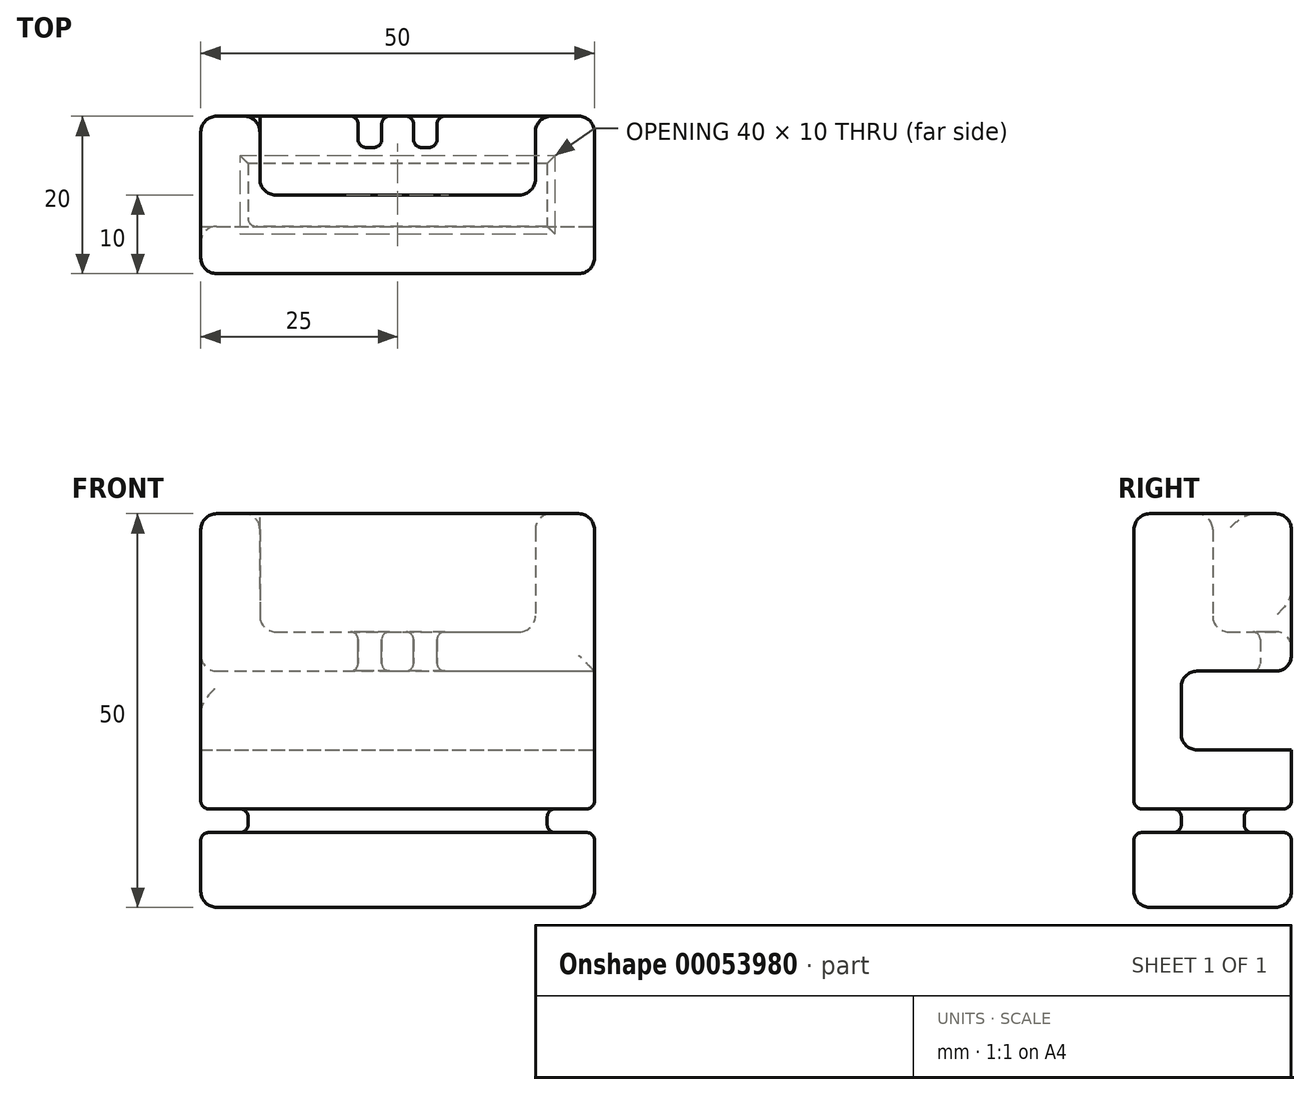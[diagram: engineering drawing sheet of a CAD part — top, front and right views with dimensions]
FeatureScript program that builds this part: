
annotation { "Feature Type Name" : "Feature", "Feature Type Description" : "" }
export const myFeature = defineFeature(function(context is Context, id is Id, definition is map)
    precondition{}
    {
        {
            var Q0;
            Q0=qCreatedBy(makeId("Front.planeOp"),FACE);
            var sketch = newSketch(context, id + "F0", { "sketchPlane" : qUnion([Q0])});
            skLineSegment(sketch, "E0.bottom", {"start": v(-25, 25) * mm, "end": v(25, 25) * mm});
            skLineSegment(sketch, "E0.top", {"start": v(-25, -25) * mm, "end": v(25, -25) * mm});
            skLineSegment(sketch, "E0.left", {"start": v(-25, 25) * mm, "end": v(-25, -25) * mm});
            skLineSegment(sketch, "E0.right", {"start": v(25, 25) * mm, "end": v(25, -25) * mm});
            skSolve(sketch);
        }
        {
            var Q0;
            Q0=makeQuery(id+"F0.imprint","IMPRINT",FACE,{"disambiguationData":[TD([[makeQuery(id+"F0.imprint","IMPRINT",EDGE,{"derivedFrom":sQuery(id+"F0.wireOp",EDGE,"E0.bottom")}),-1.0]])]});
            extrude(context, id + "F1", {"entities" : qUnion([Q0]), "endBound" : BoundingType.SYMMETRIC, "depth" : 20 * mm});
        }
        {
            var Q0;
            Q0=makeQuery(id+"F1.opExtrude","SWEPT_FACE",FACE,{"disambiguationData":[OSD([sQuery(id+"F0.wireOp",EDGE,"E0.right")])]});
            var sketch = newSketch(context, id + "F2", { "sketchPlane" : qUnion([Q0])});
            skLineSegment(sketch, "E1.bottom", {"start": v(-4, 5) * mm, "end": v(10, 5) * mm});
            skLineSegment(sketch, "E1.top", {"start": v(-4, -5) * mm, "end": v(10, -5) * mm});
            skLineSegment(sketch, "E1.left", {"start": v(-4, 5) * mm, "end": v(-4, -5) * mm});
            skLineSegment(sketch, "E1.right", {"start": v(10, 5) * mm, "end": v(10, -5) * mm});
            skSolve(sketch);
        }
        {
            var Q0;
            Q0=makeQuery(id+"F2.imprint","IMPRINT",FACE,{"disambiguationData":[TD([[makeQuery(id+"F2.imprint","IMPRINT",EDGE,{"derivedFrom":sQuery(id+"F2.wireOp",EDGE,"E1.bottom")}),-1.0]])]});
            extrude(context, id + "F3", {"entities" : qUnion([Q0]), "operationType" : NewBodyOperationType.REMOVE, "oppositeDirection" : true, "depth" : 76.7 * mm});
        }
        {
            var Q0;
            Q0=makeQuery(id+"F1.opExtrude","CAP_EDGE",EDGE,{"disambiguationData":[OSD([sQuery(id+"F0.wireOp",EDGE,"E0.bottom")])],"isStart":true});
            var Q1;
            Q1=makeQuery(id+"F3.boolean.opBoolean","COPY",EDGE,{"derivedFrom":makeQuery(id+"F3.opExtrude","SWEPT_EDGE",EDGE,{"disambiguationData":[OSD([sQuery(id+"F2.wireOp",EDGE,"E1.top"),sQuery(id+"F2.wireOp",EDGE,"E1.left")])]})});
            var Q2;
            Q2=makeQuery(id+"F3.boolean.opBoolean","COPY",EDGE,{"derivedFrom":makeQuery(id+"F3.opExtrude","SWEPT_EDGE",EDGE,{"disambiguationData":[OSD([sQuery(id+"F2.wireOp",EDGE,"E1.bottom"),sQuery(id+"F2.wireOp",EDGE,"E1.left")])]})});
            var Q3;
            Q3=makeQuery(id+"F1.opExtrude","CAP_EDGE",EDGE,{"disambiguationData":[OSD([sQuery(id+"F0.wireOp",EDGE,"E0.bottom")])],"isStart":false});
            var Q4;
            Q4=makeQuery(id+"F3.boolean.opBoolean","COPY",EDGE,{"derivedFrom":makeQuery(id+"F3.opExtrude","SWEPT_EDGE",EDGE,{"disambiguationData":[OSD([sQuery(id+"F0.wireOp",EDGE,"E0.right"),sQuery(id+"F2.wireOp",EDGE,"E1.top"),sQuery(id+"F2.wireOp",EDGE,"E1.right")])]})});
            var Q5;
            Q5=makeQuery(id+"F1.opExtrude","CAP_EDGE",EDGE,{"disambiguationData":[OSD([sQuery(id+"F0.wireOp",EDGE,"E0.top")])],"isStart":true});
            var Q6;
            Q6=makeQuery(id+"F1.opExtrude","CAP_EDGE",EDGE,{"disambiguationData":[OSD([sQuery(id+"F0.wireOp",EDGE,"E0.top")])],"isStart":false});
            var Q7;
            Q7=makeQuery(id+"F1.opExtrude","CAP_EDGE",EDGE,{"disambiguationData":[OSD([sQuery(id+"F0.wireOp",EDGE,"E0.right")])],"isStart":false});
            var Q8;
            {var subQ0=sQuery(id+"F0.wireOp",EDGE,"E0.right");var subQ1=sQuery(id+"F0.wireOp",EDGE,"E0.top");Q8=makeQuery(id+"F3.boolean.opBoolean","SPLIT",EDGE,{"disambiguationData":[TD([makeQuery(id+"F1.opExtrude","SWEPT_FACE",FACE,{"disambiguationData":[OSD([subQ1])]})])],"derivedFrom":makeQuery(id+"F1.opExtrude","CAP_EDGE",EDGE,{"disambiguationData":[OSD([subQ0])],"isStart":true})});}
            var Q9;
            {var subQ0=sQuery(id+"F0.wireOp",EDGE,"E0.left");var subQ1=sQuery(id+"F0.wireOp",EDGE,"E0.top");Q9=makeQuery(id+"F3.boolean.opBoolean","SPLIT",EDGE,{"disambiguationData":[TD([makeQuery(id+"F1.opExtrude","SWEPT_FACE",FACE,{"disambiguationData":[OSD([subQ1])]})])],"derivedFrom":makeQuery(id+"F1.opExtrude","CAP_EDGE",EDGE,{"disambiguationData":[OSD([subQ0])],"isStart":true})});}
            var Q10;
            Q10=makeQuery(id+"F1.opExtrude","CAP_EDGE",EDGE,{"disambiguationData":[OSD([sQuery(id+"F0.wireOp",EDGE,"E0.left")])],"isStart":false});
            var Q11;
            {var subQ0=sQuery(id+"F0.wireOp",EDGE,"E0.bottom");var subQ1=sQuery(id+"F0.wireOp",EDGE,"E0.left");Q11=makeQuery(id+"F3.boolean.opBoolean","SPLIT",EDGE,{"disambiguationData":[TD([makeQuery(id+"F1.opExtrude","SWEPT_FACE",FACE,{"disambiguationData":[OSD([subQ0])]})])],"derivedFrom":makeQuery(id+"F1.opExtrude","CAP_EDGE",EDGE,{"disambiguationData":[OSD([subQ1])],"isStart":true})});}
            var Q12;
            Q12=makeQuery(id+"F1.opExtrude","SWEPT_EDGE",EDGE,{"disambiguationData":[OSD([sQuery(id+"F0.wireOp",EDGE,"E0.bottom"),sQuery(id+"F0.wireOp",EDGE,"E0.left")])]});
            var Q13;
            Q13=makeQuery(id+"F1.opExtrude","SWEPT_EDGE",EDGE,{"disambiguationData":[OSD([sQuery(id+"F0.wireOp",EDGE,"E0.bottom"),sQuery(id+"F0.wireOp",EDGE,"E0.right")])]});
            var Q14;
            {var subQ0=sQuery(id+"F0.wireOp",EDGE,"E0.bottom");var subQ1=sQuery(id+"F0.wireOp",EDGE,"E0.right");Q14=makeQuery(id+"F3.boolean.opBoolean","SPLIT",EDGE,{"disambiguationData":[TD([makeQuery(id+"F1.opExtrude","SWEPT_FACE",FACE,{"disambiguationData":[OSD([subQ0])]})])],"derivedFrom":makeQuery(id+"F1.opExtrude","CAP_EDGE",EDGE,{"disambiguationData":[OSD([subQ1])],"isStart":true})});}
            var Q15;
            Q15=makeQuery(id+"F3.boolean.opBoolean","COPY",EDGE,{"derivedFrom":makeQuery(id+"F3.opExtrude","CAP_EDGE",EDGE,{"disambiguationData":[OSD([sQuery(id+"F2.wireOp",EDGE,"E1.top")])],"isStart":true})});
            var Q16;
            Q16=makeQuery(id+"F3.boolean.opBoolean","COPY",EDGE,{"derivedFrom":makeQuery(id+"F3.opExtrude","SWEPT_EDGE",EDGE,{"disambiguationData":[OSD([sQuery(id+"F0.wireOp",EDGE,"E0.right"),sQuery(id+"F2.wireOp",EDGE,"E1.bottom"),sQuery(id+"F2.wireOp",EDGE,"E1.right")])]})});
            var Q17;
            Q17=makeQuery(id+"F3.boolean.opBoolean","INTERSECT",EDGE,{"derivedFrom":[makeQuery(id+"F1.opExtrude","SWEPT_FACE",FACE,{"disambiguationData":[OSD([sQuery(id+"F0.wireOp",EDGE,"E0.left")])]}),makeQuery(id+"F3.opExtrude","SWEPT_FACE",FACE,{"disambiguationData":[OSD([sQuery(id+"F2.wireOp",EDGE,"E1.bottom")])]})]});
            var Q18;
            Q18=makeQuery(id+"F1.opExtrude","SWEPT_EDGE",EDGE,{"disambiguationData":[OSD([sQuery(id+"F0.wireOp",EDGE,"E0.top"),sQuery(id+"F0.wireOp",EDGE,"E0.left")])]});
            var Q19;
            Q19=makeQuery(id+"F1.opExtrude","SWEPT_EDGE",EDGE,{"disambiguationData":[OSD([sQuery(id+"F0.wireOp",EDGE,"E0.top"),sQuery(id+"F0.wireOp",EDGE,"E0.right")])]});
            fillet(context, id + "F4", {"entities" : qUnion([Q0, Q1, Q2, Q3, Q4, Q5, Q6, Q7, Q8, Q9, Q10, Q11, Q12, Q13, Q14, Q15, Q16, Q17, Q18, Q19]), "radius" : 2 * mm, "tangentPropagation" : true, "allowEdgeOverflow" : false});
        }
        {
            var Q0;
            Q0=qCreatedBy(makeId("Right.planeOp"),FACE);
            var sketch = newSketch(context, id + "F5", { "sketchPlane" : qUnion([Q0])});
            skLineSegment(sketch, "E2.bottom", {"start": v(0, 30) * mm, "end": v(13.71, 30) * mm});
            skLineSegment(sketch, "E2.top", {"start": v(0, 10) * mm, "end": v(13.71, 10) * mm});
            skLineSegment(sketch, "E2.left", {"start": v(0, 30) * mm, "end": v(0, 10) * mm});
            skLineSegment(sketch, "E2.right", {"start": v(13.71, 30) * mm, "end": v(13.71, 10) * mm});
            skSolve(sketch);
        }
        {
            var Q0;
            Q0=makeQuery(id+"F5.imprint","IMPRINT",FACE,{"disambiguationData":[TD([[makeQuery(id+"F5.imprint","IMPRINT",EDGE,{"derivedFrom":sQuery(id+"F5.wireOp",EDGE,"E2.bottom")}),-1.0]])]});
            extrude(context, id + "F6", {"entities" : qUnion([Q0]), "operationType" : NewBodyOperationType.REMOVE, "endBound" : BoundingType.SYMMETRIC, "oppositeDirection" : true, "depth" : 35 * mm});
        }
        {
            var Q0;
            Q0=makeQuery(id+"F6.boolean.opBoolean","COPY",EDGE,{"derivedFrom":makeQuery(id+"F6.opExtrude","SWEPT_EDGE",EDGE,{"disambiguationData":[OSD([sQuery(id+"F5.wireOp",EDGE,"E2.top"),sQuery(id+"F5.wireOp",EDGE,"E2.left")])]})});
            var Q1;
            Q1=makeQuery(id+"F6.boolean.opBoolean","INTERSECT",EDGE,{"derivedFrom":[makeQuery(id+"F1.opExtrude","SWEPT_FACE",FACE,{"disambiguationData":[OSD([sQuery(id+"F0.wireOp",EDGE,"E0.bottom")])]}),makeQuery(id+"F6.opExtrude","SWEPT_FACE",FACE,{"disambiguationData":[OSD([sQuery(id+"F5.wireOp",EDGE,"E2.left")])]})]});
            var Q2;
            Q2=makeQuery(id+"F6.boolean.opBoolean","INTERSECT",EDGE,{"derivedFrom":[makeQuery(id+"F1.opExtrude","SWEPT_FACE",FACE,{"disambiguationData":[OSD([sQuery(id+"F0.wireOp",EDGE,"E0.bottom")])]}),makeQuery(id+"F6.opExtrude","CAP_FACE",FACE,{"disambiguationData":[OSD([sQuery(id+"F5.wireOp",EDGE,"E2.bottom"),sQuery(id+"F5.wireOp",EDGE,"E2.top"),sQuery(id+"F5.wireOp",EDGE,"E2.left"),sQuery(id+"F5.wireOp",EDGE,"E2.right")])],"isStart":true})]});
            var Q3;
            Q3=makeQuery(id+"F6.boolean.opBoolean","COPY",EDGE,{"derivedFrom":makeQuery(id+"F6.opExtrude","CAP_EDGE",EDGE,{"disambiguationData":[OSD([sQuery(id+"F5.wireOp",EDGE,"E2.top")])],"isStart":true})});
            var Q4;
            {var subQ0=sQuery(id+"F0.wireOp",EDGE,"E0.bottom");var subQ1=sQuery(id+"F0.wireOp",EDGE,"E0.left");var subQ2=sQuery(id+"F0.wireOp",EDGE,"E0.right");Q4=makeQuery(id+"F6.boolean.opBoolean","INTERSECT",EDGE,{"derivedFrom":[makeQuery(id+"F3.boolean.opBoolean","SPLIT",FACE,{"disambiguationData":[TD([makeQuery(id+"F1.opExtrude","SWEPT_FACE",FACE,{"disambiguationData":[OSD([subQ0])]})])],"derivedFrom":makeQuery(id+"F1.opExtrude","CAP_FACE",FACE,{"disambiguationData":[OSD([subQ0,sQuery(id+"F0.wireOp",EDGE,"E0.top"),subQ1,subQ2])],"isStart":true})}),makeQuery(id+"F6.opExtrude","SWEPT_FACE",FACE,{"disambiguationData":[OSD([sQuery(id+"F5.wireOp",EDGE,"E2.top")])]})]});}
            var Q5;
            Q5=makeQuery(id+"F6.boolean.opBoolean","COPY",EDGE,{"derivedFrom":makeQuery(id+"F6.opExtrude","CAP_EDGE",EDGE,{"disambiguationData":[OSD([sQuery(id+"F5.wireOp",EDGE,"E2.top")])],"isStart":false})});
            var Q6;
            Q6=makeQuery(id+"F6.boolean.opBoolean","COPY",EDGE,{"derivedFrom":makeQuery(id+"F6.opExtrude","CAP_EDGE",EDGE,{"disambiguationData":[OSD([sQuery(id+"F5.wireOp",EDGE,"E2.left")])],"isStart":false})});
            var Q7;
            Q7=makeQuery(id+"F6.boolean.opBoolean","COPY",EDGE,{"derivedFrom":makeQuery(id+"F6.opExtrude","CAP_EDGE",EDGE,{"disambiguationData":[OSD([sQuery(id+"F5.wireOp",EDGE,"E2.left")])],"isStart":true})});
            fillet(context, id + "F7", {"entities" : qUnion([Q0, Q1, Q2, Q3, Q4, Q5, Q6, Q7]), "radius" : 2 * mm, "tangentPropagation" : true, "allowEdgeOverflow" : false});
        }
        {
            var Q0;
            Q0=qCreatedBy(makeId("Top.planeOp"),FACE);
            var sketch = newSketch(context, id + "F8", { "sketchPlane" : qUnion([Q0])});
            skLineSegment(sketch, "E3.bottom", {"start": v(2.01, 11.8) * mm, "end": v(5.01, 11.8) * mm});
            skLineSegment(sketch, "E3.top", {"start": v(2.01, 6.04) * mm, "end": v(5.01, 6.04) * mm});
            skLineSegment(sketch, "E3.left", {"start": v(2.01, 11.8) * mm, "end": v(2.01, 6.04) * mm});
            skLineSegment(sketch, "E3.right", {"start": v(5.01, 11.8) * mm, "end": v(5.01, 6.04) * mm});
            skLineSegment(sketch, "E4.MirrorCS", {"start": v(-2.01, 6.04) * mm, "end": v(-5.01, 6.04) * mm});
            skLineSegment(sketch, "E5.MirrorCS", {"start": v(-5.01, 11.8) * mm, "end": v(-5.01, 6.04) * mm});
            skLineSegment(sketch, "E6.MirrorCS", {"start": v(-2.01, 11.8) * mm, "end": v(-5.01, 11.8) * mm});
            skLineSegment(sketch, "E7.MirrorCS", {"start": v(-2.01, 11.8) * mm, "end": v(-2.01, 6.04) * mm});
            skSolve(sketch);
        }
        {
            var Q0;
            Q0=makeQuery(id+"F8.imprint","IMPRINT",FACE,{"disambiguationData":[TD([[makeQuery(id+"F8.imprint","IMPRINT",EDGE,{"derivedFrom":sQuery(id+"F8.wireOp",EDGE,"E3.bottom")}),-1.0]])]});
            var Q1;
            Q1=makeQuery(id+"F8.imprint","IMPRINT",FACE,{"disambiguationData":[TD([[makeQuery(id+"F8.imprint","IMPRINT",EDGE,{"derivedFrom":sQuery(id+"F8.wireOp",EDGE,"E4.MirrorCS")}),-1.0]])]});
            extrude(context, id + "F9", {"entities" : qUnion([Q0, Q1]), "operationType" : NewBodyOperationType.REMOVE, "depth" : 29.72 * mm});
        }
        {
            var Q0;
            Q0=makeQuery(id+"F9.boolean.opBoolean","INTERSECT",EDGE,{"derivedFrom":[makeQuery(id+"F6.boolean.opBoolean","COPY",FACE,{"derivedFrom":makeQuery(id+"F6.opExtrude","SWEPT_FACE",FACE,{"disambiguationData":[OSD([sQuery(id+"F5.wireOp",EDGE,"E2.top")])]})}),makeQuery(id+"F9.opExtrude","SWEPT_FACE",FACE,{"disambiguationData":[OSD([sQuery(id+"F8.wireOp",EDGE,"E3.top")])]})]});
            var Q1;
            Q1=makeQuery(id+"F9.boolean.opBoolean","COPY",EDGE,{"derivedFrom":makeQuery(id+"F9.opExtrude","SWEPT_EDGE",EDGE,{"disambiguationData":[OSD([sQuery(id+"F8.wireOp",EDGE,"E3.top"),sQuery(id+"F8.wireOp",EDGE,"E3.left")])]})});
            var Q2;
            Q2=makeQuery(id+"F9.boolean.opBoolean","INTERSECT",EDGE,{"derivedFrom":[makeQuery(id+"F6.boolean.opBoolean","COPY",FACE,{"derivedFrom":makeQuery(id+"F6.opExtrude","SWEPT_FACE",FACE,{"disambiguationData":[OSD([sQuery(id+"F5.wireOp",EDGE,"E2.top")])]})}),makeQuery(id+"F9.opExtrude","SWEPT_FACE",FACE,{"disambiguationData":[OSD([sQuery(id+"F8.wireOp",EDGE,"E3.left")])]})]});
            var Q3;
            Q3=makeQuery(id+"F9.boolean.opBoolean","INTERSECT",EDGE,{"derivedFrom":[makeQuery(id+"F6.boolean.opBoolean","COPY",FACE,{"derivedFrom":makeQuery(id+"F6.opExtrude","SWEPT_FACE",FACE,{"disambiguationData":[OSD([sQuery(id+"F5.wireOp",EDGE,"E2.top")])]})}),makeQuery(id+"F9.opExtrude","SWEPT_FACE",FACE,{"disambiguationData":[OSD([sQuery(id+"F8.wireOp",EDGE,"E4.MirrorCS")])]})]});
            var Q4;
            Q4=makeQuery(id+"F9.boolean.opBoolean","INTERSECT",EDGE,{"derivedFrom":[makeQuery(id+"F6.boolean.opBoolean","COPY",FACE,{"derivedFrom":makeQuery(id+"F6.opExtrude","SWEPT_FACE",FACE,{"disambiguationData":[OSD([sQuery(id+"F5.wireOp",EDGE,"E2.top")])]})}),makeQuery(id+"F9.opExtrude","SWEPT_FACE",FACE,{"disambiguationData":[OSD([sQuery(id+"F8.wireOp",EDGE,"E5.MirrorCS")])]})]});
            var Q5;
            Q5=makeQuery(id+"F9.boolean.opBoolean","INTERSECT",EDGE,{"derivedFrom":[makeQuery(id+"F3.boolean.opBoolean","COPY",FACE,{"derivedFrom":makeQuery(id+"F3.opExtrude","SWEPT_FACE",FACE,{"disambiguationData":[OSD([sQuery(id+"F2.wireOp",EDGE,"E1.bottom")])]})}),makeQuery(id+"F9.opExtrude","SWEPT_FACE",FACE,{"disambiguationData":[OSD([sQuery(id+"F8.wireOp",EDGE,"E3.top")])]})]});
            var Q6;
            Q6=makeQuery(id+"F9.boolean.opBoolean","COPY",EDGE,{"derivedFrom":makeQuery(id+"F9.opExtrude","SWEPT_EDGE",EDGE,{"disambiguationData":[OSD([sQuery(id+"F8.wireOp",EDGE,"E3.top"),sQuery(id+"F8.wireOp",EDGE,"E3.right")])]})});
            var Q7;
            {var subQ0=sQuery(id+"F2.wireOp",EDGE,"E1.right");var subQ1=sQuery(id+"F2.wireOp",EDGE,"E1.bottom");var subQ2=sQuery(id+"F0.wireOp",EDGE,"E0.right");Q7=makeQuery(id+"F9.boolean.opBoolean","INTERSECT",EDGE,{"derivedFrom":[makeQuery(id+"F4.opFillet","BLEND_FACE",FACE,{"disambiguationData":[OSD([subQ2,subQ1,subQ0]),TDD([makeQuery(id+"F3.boolean.opBoolean","COPY",EDGE,{"derivedFrom":makeQuery(id+"F3.opExtrude","SWEPT_EDGE",EDGE,{"disambiguationData":[OSD([subQ2,subQ1,subQ0])]})})])]}),makeQuery(id+"F9.opExtrude","SWEPT_FACE",FACE,{"disambiguationData":[OSD([sQuery(id+"F8.wireOp",EDGE,"E3.right")])]})]});}
            var Q8;
            Q8=makeQuery(id+"F9.boolean.opBoolean","INTERSECT",EDGE,{"derivedFrom":[makeQuery(id+"F3.boolean.opBoolean","COPY",FACE,{"derivedFrom":makeQuery(id+"F3.opExtrude","SWEPT_FACE",FACE,{"disambiguationData":[OSD([sQuery(id+"F2.wireOp",EDGE,"E1.bottom")])]})}),makeQuery(id+"F9.opExtrude","SWEPT_FACE",FACE,{"disambiguationData":[OSD([sQuery(id+"F8.wireOp",EDGE,"E7.MirrorCS")])]})]});
            var Q9;
            Q9=makeQuery(id+"F9.boolean.opBoolean","INTERSECT",EDGE,{"derivedFrom":[makeQuery(id+"F3.boolean.opBoolean","COPY",FACE,{"derivedFrom":makeQuery(id+"F3.opExtrude","SWEPT_FACE",FACE,{"disambiguationData":[OSD([sQuery(id+"F2.wireOp",EDGE,"E1.bottom")])]})}),makeQuery(id+"F9.opExtrude","SWEPT_FACE",FACE,{"disambiguationData":[OSD([sQuery(id+"F8.wireOp",EDGE,"E4.MirrorCS")])]})]});
            var Q10;
            Q10=makeQuery(id+"F9.boolean.opBoolean","COPY",EDGE,{"derivedFrom":makeQuery(id+"F9.opExtrude","SWEPT_EDGE",EDGE,{"disambiguationData":[OSD([sQuery(id+"F8.wireOp",EDGE,"E4.MirrorCS"),sQuery(id+"F8.wireOp",EDGE,"E7.MirrorCS")])]})});
            var Q11;
            Q11=makeQuery(id+"F9.boolean.opBoolean","COPY",EDGE,{"derivedFrom":makeQuery(id+"F9.opExtrude","SWEPT_EDGE",EDGE,{"disambiguationData":[OSD([sQuery(id+"F8.wireOp",EDGE,"E4.MirrorCS"),sQuery(id+"F8.wireOp",EDGE,"E5.MirrorCS")])]})});
            fillet(context, id + "F10", {"entities" : qUnion([Q0, Q1, Q2, Q3, Q4, Q5, Q6, Q7, Q8, Q9, Q10, Q11]), "radius" : 1 * mm, "tangentPropagation" : true, "allowEdgeOverflow" : false});
        }
        {
            var Q0;
            {var subQ0=sQuery(id+"F0.wireOp",EDGE,"E0.top");var subQ1=sQuery(id+"F0.wireOp",EDGE,"E0.left");var subQ2=sQuery(id+"F0.wireOp",EDGE,"E0.right");Q0=makeQuery(id+"F3.boolean.opBoolean","SPLIT",FACE,{"disambiguationData":[TD([makeQuery(id+"F1.opExtrude","SWEPT_FACE",FACE,{"disambiguationData":[OSD([subQ0])]})])],"derivedFrom":makeQuery(id+"F1.opExtrude","CAP_FACE",FACE,{"disambiguationData":[OSD([sQuery(id+"F0.wireOp",EDGE,"E0.bottom"),subQ0,subQ1,subQ2])],"isStart":true})});}
            var sketch = newSketch(context, id + "F11", { "sketchPlane" : qUnion([Q0])});
            skLineSegment(sketch, "E8.bottom", {"start": v(-25, -12.5) * mm, "end": v(25, -12.5) * mm});
            skLineSegment(sketch, "E8.top", {"start": v(-25, -15.5) * mm, "end": v(25, -15.5) * mm});
            skLineSegment(sketch, "E8.left", {"start": v(-25, -12.5) * mm, "end": v(-25, -15.5) * mm});
            skLineSegment(sketch, "E8.right", {"start": v(25, -12.5) * mm, "end": v(25, -15.5) * mm});
            skSolve(sketch);
        }
        {
            var Q0;
            {var subQ0=sQuery(id+"F11.wireOp",EDGE,"E8.bottom");var subQ1=sQuery(id+"F0.wireOp",EDGE,"E0.top");var subQ2=makeQuery(id+"F1.opExtrude","SWEPT_FACE",FACE,{"disambiguationData":[OSD([subQ1])]});var subQ3=sQuery(id+"F0.wireOp",EDGE,"E0.left");var subQ5=sQuery(id+"F0.wireOp",EDGE,"E0.right");var subQ8=makeQuery(id+"F1.opExtrude","CAP_FACE",FACE,{"disambiguationData":[OSD([sQuery(id+"F0.wireOp",EDGE,"E0.bottom"),subQ1,subQ3,subQ5])],"isStart":true});var subQ9=makeQuery(id+"F3.boolean.opBoolean","SPLIT",FACE,{"disambiguationData":[TD([subQ2])],"derivedFrom":subQ8});var subQ10=makeQuery(id+"F4.opFillet","BLEND_EDGE",EDGE,{"blendedFrom":[makeQuery(id+"F3.boolean.opBoolean","SPLIT",EDGE,{"disambiguationData":[TD([subQ2])],"derivedFrom":makeQuery(id+"F1.opExtrude","CAP_EDGE",EDGE,{"disambiguationData":[OSD([subQ5])],"isStart":true})}),subQ9],"blendedInto":[subQ9]});var subQ11=makeQuery(id+"F11.imprint","INTERSECT",VERTEX,{"derivedFrom":[subQ10,subQ0]});Q0=makeQuery(id+"F11.imprint","IMPRINT",FACE,{"disambiguationData":[TD([[makeQuery(id+"F11.imprint","IMPRINT",EDGE,{"disambiguationData":[TD([[subQ11,-1.0]])],"derivedFrom":subQ0}),-1.0]])]});}
            var Q1;
            {var subQ0=sQuery(id+"F11.wireOp",EDGE,"E8.left");Q1=makeQuery(id+"F11.imprint","IMPRINT",FACE,{"disambiguationData":[TD([[makeQuery(id+"F11.imprint","IMPRINT",EDGE,{"derivedFrom":subQ0}),1.0]])]});}
            var Q2;
            {var subQ0=sQuery(id+"F11.wireOp",EDGE,"E8.right");Q2=makeQuery(id+"F11.imprint","IMPRINT",FACE,{"disambiguationData":[TD([[makeQuery(id+"F11.imprint","IMPRINT",EDGE,{"derivedFrom":subQ0}),-1.0]])]});}
            extrude(context, id + "F12", {"entities" : qUnion([Q0, Q1, Q2]), "operationType" : NewBodyOperationType.REMOVE, "oppositeDirection" : true, "depth" : 6 * mm});
        }
        {
            var Q0;
            Q0=makeQuery(id+"F1.opExtrude","SWEPT_FACE",FACE,{"disambiguationData":[OSD([sQuery(id+"F0.wireOp",EDGE,"E0.right")])]});
            var sketch = newSketch(context, id + "F13", { "sketchPlane" : qUnion([Q0])});
            skLineSegment(sketch, "E9.bottom", {"start": v(4, -15.5) * mm, "end": v(-15.57, -15.5) * mm});
            skLineSegment(sketch, "E9.top", {"start": v(4, -12.5) * mm, "end": v(-15.57, -12.5) * mm});
            skLineSegment(sketch, "E9.left", {"start": v(4, -15.5) * mm, "end": v(4, -12.5) * mm});
            skLineSegment(sketch, "E9.right", {"start": v(-15.57, -15.5) * mm, "end": v(-15.57, -12.5) * mm});
            skSolve(sketch);
        }
        {
            var Q0;
            {var subQ0=sQuery(id+"F13.wireOp",EDGE,"E9.right");Q0=makeQuery(id+"F13.imprint","IMPRINT",FACE,{"disambiguationData":[TD([[makeQuery(id+"F13.imprint","IMPRINT",EDGE,{"derivedFrom":subQ0}),-1.0]])]});}
            var Q1;
            {var subQ0=sQuery(id+"F13.wireOp",EDGE,"E9.left");Q1=makeQuery(id+"F13.imprint","IMPRINT",FACE,{"disambiguationData":[TD([[makeQuery(id+"F13.imprint","IMPRINT",EDGE,{"derivedFrom":subQ0}),-1.0]])]});}
            extrude(context, id + "F14", {"entities" : qUnion([Q0, Q1]), "operationType" : NewBodyOperationType.REMOVE, "oppositeDirection" : true, "depth" : 6 * mm});
        }
        {
            var Q0;
            Q0=makeQuery(id+"F1.opExtrude","CAP_FACE",FACE,{"disambiguationData":[OSD([sQuery(id+"F0.wireOp",EDGE,"E0.bottom"),sQuery(id+"F0.wireOp",EDGE,"E0.top"),sQuery(id+"F0.wireOp",EDGE,"E0.left"),sQuery(id+"F0.wireOp",EDGE,"E0.right")])],"isStart":false});
            var sketch = newSketch(context, id + "F15", { "sketchPlane" : qUnion([Q0])});
            skLineSegment(sketch, "E10.bottom", {"start": v(19, -15.5) * mm, "end": v(-31.6, -15.5) * mm});
            skLineSegment(sketch, "E10.top", {"start": v(19, -12.5) * mm, "end": v(-31.6, -12.5) * mm});
            skLineSegment(sketch, "E10.left", {"start": v(19, -15.5) * mm, "end": v(19, -12.5) * mm});
            skLineSegment(sketch, "E10.right", {"start": v(-31.6, -15.5) * mm, "end": v(-31.6, -12.5) * mm});
            skSolve(sketch);
        }
        {
            var Q0;
            {var subQ0=sQuery(id+"F15.wireOp",EDGE,"E10.right");Q0=makeQuery(id+"F15.imprint","IMPRINT",FACE,{"disambiguationData":[TD([[makeQuery(id+"F15.imprint","IMPRINT",EDGE,{"derivedFrom":subQ0}),-1.0]])]});}
            var Q1;
            {var subQ0=sQuery(id+"F15.wireOp",EDGE,"E10.left");Q1=makeQuery(id+"F15.imprint","IMPRINT",FACE,{"disambiguationData":[TD([[makeQuery(id+"F15.imprint","IMPRINT",EDGE,{"derivedFrom":subQ0}),1.0]])]});}
            extrude(context, id + "F16", {"entities" : qUnion([Q0, Q1]), "operationType" : NewBodyOperationType.REMOVE, "oppositeDirection" : true, "depth" : 6 * mm});
        }
        {
            var Q0;
            Q0=makeQuery(id+"F1.opExtrude","SWEPT_FACE",FACE,{"disambiguationData":[OSD([sQuery(id+"F0.wireOp",EDGE,"E0.left")])]});
            var sketch = newSketch(context, id + "F17", { "sketchPlane" : qUnion([Q0])});
            skLineSegment(sketch, "E11.bottom", {"start": v(-4, -12.5) * mm, "end": v(13.16, -12.5) * mm});
            skLineSegment(sketch, "E11.top", {"start": v(-4, -15.5) * mm, "end": v(13.16, -15.5) * mm});
            skLineSegment(sketch, "E11.left", {"start": v(-4, -12.5) * mm, "end": v(-4, -15.5) * mm});
            skLineSegment(sketch, "E11.right", {"start": v(13.16, -12.5) * mm, "end": v(13.16, -15.5) * mm});
            skSolve(sketch);
        }
        {
            var Q0;
            {var subQ0=sQuery(id+"F17.wireOp",EDGE,"E11.left");Q0=makeQuery(id+"F17.imprint","IMPRINT",FACE,{"disambiguationData":[TD([[makeQuery(id+"F17.imprint","IMPRINT",EDGE,{"derivedFrom":subQ0}),1.0]])]});}
            var Q1;
            {var subQ15=sQuery(id+"F17.wireOp",EDGE,"E11.right");Q1=makeQuery(id+"F17.imprint","IMPRINT",FACE,{"disambiguationData":[TD([[makeQuery(id+"F17.imprint","IMPRINT",EDGE,{"derivedFrom":subQ15}),-1.0]])]});}
            extrude(context, id + "F18", {"entities" : qUnion([Q0, Q1]), "operationType" : NewBodyOperationType.REMOVE, "oppositeDirection" : true, "depth" : 6 * mm});
        }
        {
            var Q0;
            Q0=makeQuery(id+"F12.boolean.opBoolean","COPY",EDGE,{"derivedFrom":makeQuery(id+"F12.opExtrude","CAP_EDGE",EDGE,{"disambiguationData":[OSD([sQuery(id+"F11.wireOp",EDGE,"E8.top")])],"isStart":true})});
            var Q1;
            Q1=makeQuery(id+"F12.boolean.opBoolean","COPY",EDGE,{"derivedFrom":makeQuery(id+"F12.opExtrude","CAP_EDGE",EDGE,{"disambiguationData":[OSD([sQuery(id+"F11.wireOp",EDGE,"E8.top")])],"isStart":false})});
            var Q2;
            Q2=makeQuery(id+"F14.boolean.opBoolean","COPY",EDGE,{"derivedFrom":makeQuery(id+"F14.opExtrude","CAP_EDGE",EDGE,{"disambiguationData":[OSD([sQuery(id+"F13.wireOp",EDGE,"E9.top")])],"isStart":false})});
            var Q3;
            Q3=makeQuery(id+"F12.boolean.opBoolean","COPY",EDGE,{"derivedFrom":makeQuery(id+"F12.opExtrude","CAP_EDGE",EDGE,{"disambiguationData":[OSD([sQuery(id+"F11.wireOp",EDGE,"E8.bottom")])],"isStart":false})});
            var Q4;
            Q4=makeQuery(id+"F12.boolean.opBoolean","COPY",EDGE,{"derivedFrom":makeQuery(id+"F12.opExtrude","CAP_EDGE",EDGE,{"disambiguationData":[OSD([sQuery(id+"F11.wireOp",EDGE,"E8.bottom")])],"isStart":true})});
            var Q5;
            {var subQ0=sQuery(id+"F0.wireOp",EDGE,"E0.right");var subQ1=sQuery(id+"F0.wireOp",EDGE,"E0.top");Q5=makeQuery(id+"F12.boolean.opBoolean","INTERSECT",EDGE,{"derivedFrom":[makeQuery(id+"F4.opFillet","BLEND_FACE",FACE,{"disambiguationData":[OSD([subQ0]),TDD([makeQuery(id+"F3.boolean.opBoolean","SPLIT",EDGE,{"disambiguationData":[TD([makeQuery(id+"F1.opExtrude","SWEPT_FACE",FACE,{"disambiguationData":[OSD([subQ1])]})])],"derivedFrom":makeQuery(id+"F1.opExtrude","CAP_EDGE",EDGE,{"disambiguationData":[OSD([subQ0])],"isStart":true})})])]}),makeQuery(id+"F12.opExtrude","SWEPT_FACE",FACE,{"disambiguationData":[OSD([sQuery(id+"F11.wireOp",EDGE,"E8.bottom")])]})]});}
            var Q6;
            Q6=makeQuery(id+"F14.boolean.opBoolean","MERGE",EDGE,{"derivedFrom":[makeQuery(id+"F12.boolean.opBoolean","COPY",EDGE,{"derivedFrom":makeQuery(id+"F12.opExtrude","SWEPT_EDGE",EDGE,{"disambiguationData":[OSD([sQuery(id+"F11.wireOp",EDGE,"E8.bottom"),sQuery(id+"F11.wireOp",EDGE,"E8.left")])]})}),makeQuery(id+"F14.opExtrude","CAP_EDGE",EDGE,{"disambiguationData":[OSD([sQuery(id+"F13.wireOp",EDGE,"E9.top")])],"isStart":true})]});
            var Q7;
            Q7=makeQuery(id+"F14.boolean.opBoolean","COPY",EDGE,{"derivedFrom":makeQuery(id+"F14.opExtrude","CAP_EDGE",EDGE,{"disambiguationData":[OSD([sQuery(id+"F13.wireOp",EDGE,"E9.left")])],"isStart":false})});
            var Q8;
            Q8=makeQuery(id+"F14.boolean.opBoolean","COPY",EDGE,{"derivedFrom":makeQuery(id+"F14.opExtrude","CAP_EDGE",EDGE,{"disambiguationData":[OSD([sQuery(id+"F13.wireOp",EDGE,"E9.bottom")])],"isStart":false})});
            var Q9;
            Q9=makeQuery(id+"F14.boolean.opBoolean","MERGE",EDGE,{"derivedFrom":[makeQuery(id+"F12.boolean.opBoolean","COPY",EDGE,{"derivedFrom":makeQuery(id+"F12.opExtrude","SWEPT_EDGE",EDGE,{"disambiguationData":[OSD([sQuery(id+"F11.wireOp",EDGE,"E8.top"),sQuery(id+"F11.wireOp",EDGE,"E8.left")])]})}),makeQuery(id+"F14.opExtrude","CAP_EDGE",EDGE,{"disambiguationData":[OSD([sQuery(id+"F13.wireOp",EDGE,"E9.bottom")])],"isStart":true})]});
            var Q10;
            {var subQ0=sQuery(id+"F0.wireOp",EDGE,"E0.right");var subQ1=sQuery(id+"F0.wireOp",EDGE,"E0.top");Q10=makeQuery(id+"F12.boolean.opBoolean","INTERSECT",EDGE,{"derivedFrom":[makeQuery(id+"F4.opFillet","BLEND_FACE",FACE,{"disambiguationData":[OSD([subQ0]),TDD([makeQuery(id+"F3.boolean.opBoolean","SPLIT",EDGE,{"disambiguationData":[TD([makeQuery(id+"F1.opExtrude","SWEPT_FACE",FACE,{"disambiguationData":[OSD([subQ1])]})])],"derivedFrom":makeQuery(id+"F1.opExtrude","CAP_EDGE",EDGE,{"disambiguationData":[OSD([subQ0])],"isStart":true})})])]}),makeQuery(id+"F12.opExtrude","SWEPT_FACE",FACE,{"disambiguationData":[OSD([sQuery(id+"F11.wireOp",EDGE,"E8.top")])]})]});}
            var Q11;
            {var subQ0=sQuery(id+"F0.wireOp",EDGE,"E0.right");Q11=makeQuery(id+"F14.boolean.opBoolean","INTERSECT",EDGE,{"derivedFrom":[makeQuery(id+"F4.opFillet","BLEND_FACE",FACE,{"disambiguationData":[OSD([subQ0]),TDD([makeQuery(id+"F1.opExtrude","CAP_EDGE",EDGE,{"disambiguationData":[OSD([subQ0])],"isStart":false})])]}),makeQuery(id+"F14.opExtrude","SWEPT_FACE",FACE,{"disambiguationData":[OSD([sQuery(id+"F13.wireOp",EDGE,"E9.bottom")])]})]});}
            var Q12;
            Q12=makeQuery(id+"F16.boolean.opBoolean","COPY",EDGE,{"derivedFrom":makeQuery(id+"F16.opExtrude","CAP_EDGE",EDGE,{"disambiguationData":[OSD([sQuery(id+"F15.wireOp",EDGE,"E10.bottom")])],"isStart":false})});
            var Q13;
            Q13=makeQuery(id+"F16.boolean.opBoolean","MERGE",EDGE,{"derivedFrom":[makeQuery(id+"F14.boolean.opBoolean","INTERSECT",EDGE,{"derivedFrom":[makeQuery(id+"F1.opExtrude","CAP_FACE",FACE,{"disambiguationData":[OSD([sQuery(id+"F0.wireOp",EDGE,"E0.bottom"),sQuery(id+"F0.wireOp",EDGE,"E0.top"),sQuery(id+"F0.wireOp",EDGE,"E0.left"),sQuery(id+"F0.wireOp",EDGE,"E0.right")])],"isStart":false}),makeQuery(id+"F14.opExtrude","SWEPT_FACE",FACE,{"disambiguationData":[OSD([sQuery(id+"F13.wireOp",EDGE,"E9.bottom")])]})]}),makeQuery(id+"F16.opExtrude","CAP_EDGE",EDGE,{"disambiguationData":[OSD([sQuery(id+"F15.wireOp",EDGE,"E10.bottom")])],"isStart":true})]});
            var Q14;
            Q14=makeQuery(id+"F16.boolean.opBoolean","COPY",EDGE,{"derivedFrom":makeQuery(id+"F16.opExtrude","CAP_EDGE",EDGE,{"disambiguationData":[OSD([sQuery(id+"F15.wireOp",EDGE,"E10.top")])],"isStart":false})});
            var Q15;
            Q15=makeQuery(id+"F16.boolean.opBoolean","MERGE",EDGE,{"derivedFrom":[makeQuery(id+"F14.boolean.opBoolean","INTERSECT",EDGE,{"derivedFrom":[makeQuery(id+"F1.opExtrude","CAP_FACE",FACE,{"disambiguationData":[OSD([sQuery(id+"F0.wireOp",EDGE,"E0.bottom"),sQuery(id+"F0.wireOp",EDGE,"E0.top"),sQuery(id+"F0.wireOp",EDGE,"E0.left"),sQuery(id+"F0.wireOp",EDGE,"E0.right")])],"isStart":false}),makeQuery(id+"F14.opExtrude","SWEPT_FACE",FACE,{"disambiguationData":[OSD([sQuery(id+"F13.wireOp",EDGE,"E9.top")])]})]}),makeQuery(id+"F16.opExtrude","CAP_EDGE",EDGE,{"disambiguationData":[OSD([sQuery(id+"F15.wireOp",EDGE,"E10.top")])],"isStart":true})]});
            var Q16;
            Q16=makeQuery(id+"F18.boolean.opBoolean","COPY",EDGE,{"derivedFrom":makeQuery(id+"F18.opExtrude","CAP_EDGE",EDGE,{"disambiguationData":[OSD([sQuery(id+"F17.wireOp",EDGE,"E11.bottom")])],"isStart":false})});
            var Q17;
            Q17=makeQuery(id+"F18.boolean.opBoolean","MERGE",EDGE,{"derivedFrom":[makeQuery(id+"F12.boolean.opBoolean","COPY",EDGE,{"derivedFrom":makeQuery(id+"F12.opExtrude","SWEPT_EDGE",EDGE,{"disambiguationData":[OSD([sQuery(id+"F11.wireOp",EDGE,"E8.bottom"),sQuery(id+"F11.wireOp",EDGE,"E8.right")])]})}),makeQuery(id+"F16.boolean.opBoolean","INTERSECT",EDGE,{"derivedFrom":[makeQuery(id+"F1.opExtrude","SWEPT_FACE",FACE,{"disambiguationData":[OSD([sQuery(id+"F0.wireOp",EDGE,"E0.left")])]}),makeQuery(id+"F16.opExtrude","SWEPT_FACE",FACE,{"disambiguationData":[OSD([sQuery(id+"F15.wireOp",EDGE,"E10.top")])]})]}),makeQuery(id+"F18.opExtrude","CAP_EDGE",EDGE,{"disambiguationData":[OSD([sQuery(id+"F17.wireOp",EDGE,"E11.bottom")])],"isStart":true})]});
            var Q18;
            {var subQ0=sQuery(id+"F0.wireOp",EDGE,"E0.left");Q18=makeQuery(id+"F16.boolean.opBoolean","INTERSECT",EDGE,{"derivedFrom":[makeQuery(id+"F4.opFillet","BLEND_FACE",FACE,{"disambiguationData":[OSD([subQ0]),TDD([makeQuery(id+"F1.opExtrude","CAP_EDGE",EDGE,{"disambiguationData":[OSD([subQ0])],"isStart":false})])]}),makeQuery(id+"F16.opExtrude","SWEPT_FACE",FACE,{"disambiguationData":[OSD([sQuery(id+"F15.wireOp",EDGE,"E10.top")])]})]});}
            var Q19;
            Q19=makeQuery(id+"F18.boolean.opBoolean","INTERSECT",EDGE,{"derivedFrom":[makeQuery(id+"F16.boolean.opBoolean","COPY",FACE,{"derivedFrom":makeQuery(id+"F16.opExtrude","CAP_FACE",FACE,{"disambiguationData":[OSD([sQuery(id+"F15.wireOp",EDGE,"E10.bottom"),sQuery(id+"F15.wireOp",EDGE,"E10.top"),sQuery(id+"F15.wireOp",EDGE,"E10.left"),sQuery(id+"F15.wireOp",EDGE,"E10.right")])],"isStart":false})}),makeQuery(id+"F18.opExtrude","CAP_FACE",FACE,{"disambiguationData":[OSD([sQuery(id+"F17.wireOp",EDGE,"E11.bottom"),sQuery(id+"F17.wireOp",EDGE,"E11.top"),sQuery(id+"F17.wireOp",EDGE,"E11.left"),sQuery(id+"F17.wireOp",EDGE,"E11.right")])],"isStart":false})]});
            var Q20;
            Q20=makeQuery(id+"F18.boolean.opBoolean","COPY",EDGE,{"derivedFrom":makeQuery(id+"F18.opExtrude","CAP_EDGE",EDGE,{"disambiguationData":[OSD([sQuery(id+"F17.wireOp",EDGE,"E11.left")])],"isStart":false})});
            var Q21;
            Q21=makeQuery(id+"F18.boolean.opBoolean","COPY",EDGE,{"derivedFrom":makeQuery(id+"F18.opExtrude","CAP_EDGE",EDGE,{"disambiguationData":[OSD([sQuery(id+"F17.wireOp",EDGE,"E11.top")])],"isStart":false})});
            var Q22;
            {var subQ0=sQuery(id+"F0.wireOp",EDGE,"E0.left");var subQ1=sQuery(id+"F0.wireOp",EDGE,"E0.top");Q22=makeQuery(id+"F12.boolean.opBoolean","INTERSECT",EDGE,{"derivedFrom":[makeQuery(id+"F4.opFillet","BLEND_FACE",FACE,{"disambiguationData":[OSD([subQ0]),TDD([makeQuery(id+"F3.boolean.opBoolean","SPLIT",EDGE,{"disambiguationData":[TD([makeQuery(id+"F1.opExtrude","SWEPT_FACE",FACE,{"disambiguationData":[OSD([subQ1])]})])],"derivedFrom":makeQuery(id+"F1.opExtrude","CAP_EDGE",EDGE,{"disambiguationData":[OSD([subQ0])],"isStart":true})})])]}),makeQuery(id+"F12.opExtrude","SWEPT_FACE",FACE,{"disambiguationData":[OSD([sQuery(id+"F11.wireOp",EDGE,"E8.top")])]})]});}
            var Q23;
            Q23=makeQuery(id+"F18.boolean.opBoolean","MERGE",EDGE,{"derivedFrom":[makeQuery(id+"F12.boolean.opBoolean","COPY",EDGE,{"derivedFrom":makeQuery(id+"F12.opExtrude","SWEPT_EDGE",EDGE,{"disambiguationData":[OSD([sQuery(id+"F11.wireOp",EDGE,"E8.top"),sQuery(id+"F11.wireOp",EDGE,"E8.right")])]})}),makeQuery(id+"F16.boolean.opBoolean","INTERSECT",EDGE,{"derivedFrom":[makeQuery(id+"F1.opExtrude","SWEPT_FACE",FACE,{"disambiguationData":[OSD([sQuery(id+"F0.wireOp",EDGE,"E0.left")])]}),makeQuery(id+"F16.opExtrude","SWEPT_FACE",FACE,{"disambiguationData":[OSD([sQuery(id+"F15.wireOp",EDGE,"E10.bottom")])]})]}),makeQuery(id+"F18.opExtrude","CAP_EDGE",EDGE,{"disambiguationData":[OSD([sQuery(id+"F17.wireOp",EDGE,"E11.top")])],"isStart":true})]});
            var Q24;
            {var subQ0=sQuery(id+"F0.wireOp",EDGE,"E0.left");Q24=makeQuery(id+"F16.boolean.opBoolean","INTERSECT",EDGE,{"derivedFrom":[makeQuery(id+"F4.opFillet","BLEND_FACE",FACE,{"disambiguationData":[OSD([subQ0]),TDD([makeQuery(id+"F1.opExtrude","CAP_EDGE",EDGE,{"disambiguationData":[OSD([subQ0])],"isStart":false})])]}),makeQuery(id+"F16.opExtrude","SWEPT_FACE",FACE,{"disambiguationData":[OSD([sQuery(id+"F15.wireOp",EDGE,"E10.bottom")])]})]});}
            var Q25;
            {var subQ0=sQuery(id+"F0.wireOp",EDGE,"E0.left");var subQ1=sQuery(id+"F0.wireOp",EDGE,"E0.top");Q25=makeQuery(id+"F12.boolean.opBoolean","INTERSECT",EDGE,{"derivedFrom":[makeQuery(id+"F4.opFillet","BLEND_FACE",FACE,{"disambiguationData":[OSD([subQ0]),TDD([makeQuery(id+"F3.boolean.opBoolean","SPLIT",EDGE,{"disambiguationData":[TD([makeQuery(id+"F1.opExtrude","SWEPT_FACE",FACE,{"disambiguationData":[OSD([subQ1])]})])],"derivedFrom":makeQuery(id+"F1.opExtrude","CAP_EDGE",EDGE,{"disambiguationData":[OSD([subQ0])],"isStart":true})})])]}),makeQuery(id+"F12.opExtrude","SWEPT_FACE",FACE,{"disambiguationData":[OSD([sQuery(id+"F11.wireOp",EDGE,"E8.bottom")])]})]});}
            var Q26;
            Q26=makeQuery(id+"F16.boolean.opBoolean","COPY",EDGE,{"derivedFrom":makeQuery(id+"F16.opExtrude","CAP_EDGE",EDGE,{"disambiguationData":[OSD([sQuery(id+"F15.wireOp",EDGE,"E10.left")])],"isStart":false})});
            fillet(context, id + "F19", {"entities" : qUnion([Q0, Q1, Q2, Q3, Q4, Q5, Q6, Q7, Q8, Q9, Q10, Q11, Q12, Q13, Q14, Q15, Q16, Q17, Q18, Q19, Q20, Q21, Q22, Q23, Q24, Q25, Q26]), "radius" : 1 * mm, "tangentPropagation" : true, "allowEdgeOverflow" : false});
        }
    });
